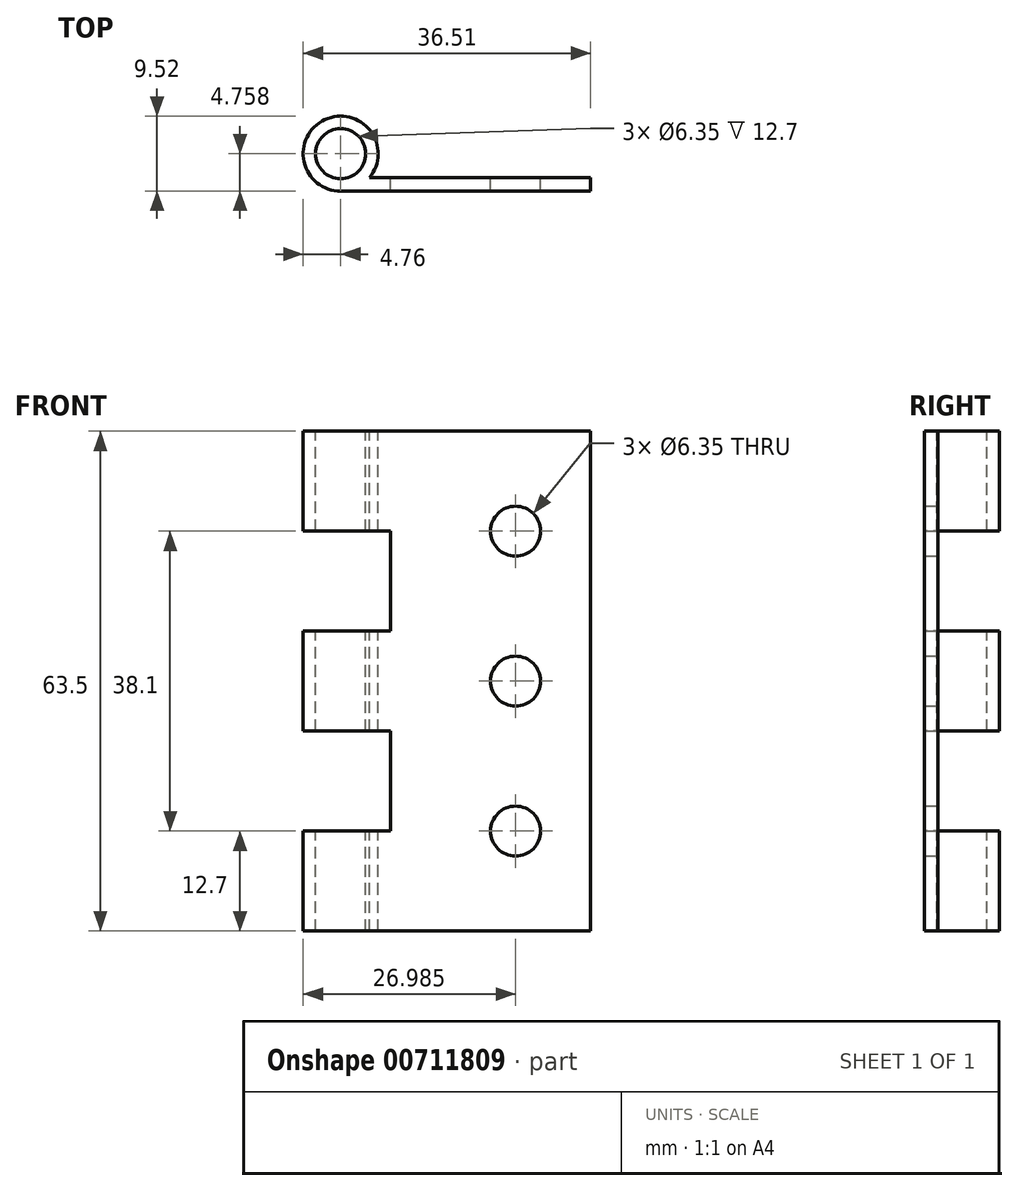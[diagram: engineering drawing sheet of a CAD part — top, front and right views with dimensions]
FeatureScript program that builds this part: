
annotation { "Feature Type Name" : "Feature", "Feature Type Description" : "" }
export const myFeature = defineFeature(function(context is Context, id is Id, definition is map)
    precondition{}
    {
        {
            var Q0;
            Q0=qCreatedBy(makeId("Front.planeOp"),FACE);
            var sketch = newSketch(context, id + "F0", { "sketchPlane" : qUnion([Q0])});
            skLineSegment(sketch, "E0.bottom", {"start": v(0, 0) * mm, "end": v(25.4, 0) * mm});
            skLineSegment(sketch, "E0.top", {"start": v(0, 63.5) * mm, "end": v(25.4, 63.5) * mm});
            skLineSegment(sketch, "E0.left", {"start": v(0, 0) * mm, "end": v(0, 63.5) * mm});
            skLineSegment(sketch, "E0.right", {"start": v(25.4, 0) * mm, "end": v(25.4, 63.5) * mm});
            skLineSegment(sketch, "E1.bottom", {"start": v(0, 63.5) * mm, "end": v(-9.53, 63.5) * mm});
            skLineSegment(sketch, "E1.top", {"start": v(0, 50.8) * mm, "end": v(-9.53, 50.8) * mm});
            skLineSegment(sketch, "E1.left", {"start": v(0, 63.5) * mm, "end": v(0, 50.8) * mm});
            skLineSegment(sketch, "E1.right", {"start": v(-9.53, 63.5) * mm, "end": v(-9.53, 50.8) * mm});
            skLineSegment(sketch, "E2.bottom", {"start": v(0, 0) * mm, "end": v(-9.52, 0) * mm});
            skLineSegment(sketch, "E2.top", {"start": v(0, 12.7) * mm, "end": v(-9.53, 12.7) * mm});
            skLineSegment(sketch, "E2.left", {"start": v(0, 0) * mm, "end": v(0, 12.7) * mm});
            skLineSegment(sketch, "E2.right", {"start": v(-9.52, 0) * mm, "end": v(-9.53, 12.7) * mm});
            skLineSegment(sketch, "E3.bottom", {"start": v(0, 38.1) * mm, "end": v(-9.53, 38.1) * mm});
            skLineSegment(sketch, "E3.top", {"start": v(0, 25.4) * mm, "end": v(-9.53, 25.4) * mm});
            skLineSegment(sketch, "E3.left", {"start": v(0, 38.1) * mm, "end": v(0, 25.4) * mm});
            skLineSegment(sketch, "E3.right", {"start": v(-9.53, 38.1) * mm, "end": v(-9.53, 25.4) * mm});
            skCircle(sketch, "E4", {"center": v(15.87, 50.8) * mm, "radius": 3.18 * mm});
            skCircle(sketch, "E5", {"center": v(15.88, 31.75) * mm, "radius": 3.18 * mm});
            skCircle(sketch, "E6", {"center": v(15.88, 12.7) * mm, "radius": 3.18 * mm});
            skSolve(sketch);
        }
        {
            var Q0;
            Q0 = qSketchRegion(id + "F0", true);
            extrude(context, id + "F1", {"entities" : qUnion([Q0]), "depth" : 1.71 * mm, "offsetDistance" : 25.4 * mm});
        }
        {
            var Q0;
            Q0=makeQuery(id+"F1.opExtrude","SWEPT_FACE",FACE,{"disambiguationData":[OSD([sQuery(id+"F0.wireOp",EDGE,"E0.top"),sQuery(id+"F0.wireOp",EDGE,"E1.bottom")])]});
            var sketch = newSketch(context, id + "F2", { "sketchPlane" : qUnion([Q0])});
            skCircle(sketch, "E7", {"center": v(-6.35, 3.05) * mm, "radius": 4.76 * mm});
            skSolve(sketch);
        }
        {
            var Q0;
            Q0 = qSketchRegion(id + "F2", true);
            extrude(context, id + "F3", {"entities" : qUnion([Q0]), "operationType" : NewBodyOperationType.ADD, "oppositeDirection" : true, "depth" : 63.5 * mm, "offsetDistance" : 25.4 * mm});
        }
        {
            var Q0;
            Q0=makeQuery(id+"F3.boolean.opBoolean","MERGE",FACE,{"derivedFrom":[makeQuery(id+"F1.opExtrude","SWEPT_FACE",FACE,{"disambiguationData":[OSD([sQuery(id+"F0.wireOp",EDGE,"E0.top"),sQuery(id+"F0.wireOp",EDGE,"E1.bottom")])]}),makeQuery(id+"F3.opExtrude","CAP_FACE",FACE,{"disambiguationData":[OSD([sQuery(id+"F2.wireOp",EDGE,"E7")])],"isStart":true})]});
            var sketch = newSketch(context, id + "F4", { "sketchPlane" : qUnion([Q0])});
            skArc(sketch, "E8", {"start": v(-9.53, -0.5) * mm, "mid": v(-8.05, -1.4) * mm, "end": v(-6.35, -1.71) * mm});
            skLineSegment(sketch, "E9", {"start": v(-9.53, -1.71) * mm, "end": v(-9.53, -0.5) * mm});
            skLineSegment(sketch, "E10", {"start": v(-9.53, -1.71) * mm, "end": v(-6.35, -1.71) * mm});
            skCircle(sketch, "E11", {"center": v(-6.35, 3.05) * mm, "radius": 3.18 * mm});
            skSolve(sketch);
        }
        {
            var Q0;
            Q0=makeQuery(id+"F4.imprint","IMPRINT",FACE,{"disambiguationData":[TD([[makeQuery(id+"F4.imprint","IMPRINT",EDGE,{"derivedFrom":sQuery(id+"F4.wireOp",EDGE,"E8")}),-1.0]])]});
            var Q1;
            Q1=makeQuery(id+"F4.imprint","IMPRINT",FACE,{"disambiguationData":[TD([[makeQuery(id+"F4.imprint","IMPRINT",EDGE,{"derivedFrom":sQuery(id+"F4.wireOp",EDGE,"E11")}),1.0]])]});
            extrude(context, id + "F5", {"entities" : qUnion([Q0, Q1]), "operationType" : NewBodyOperationType.REMOVE, "endBound" : BoundingType.THROUGH_ALL, "oppositeDirection" : true, "depth" : 25.4 * mm, "offsetDistance" : 25.4 * mm});
        }
        {
            var Q0;
            Q0=makeQuery(id+"F1.opExtrude","CAP_FACE",FACE,{"disambiguationData":[OSD([sQuery(id+"F0.wireOp",EDGE,"E0.bottom"),sQuery(id+"F0.wireOp",EDGE,"E0.top"),sQuery(id+"F0.wireOp",EDGE,"E0.left"),sQuery(id+"F0.wireOp",EDGE,"E0.right"),sQuery(id+"F0.wireOp",EDGE,"E1.bottom"),sQuery(id+"F0.wireOp",EDGE,"E1.top"),sQuery(id+"F0.wireOp",EDGE,"E1.right"),sQuery(id+"F0.wireOp",EDGE,"E2.bottom"),sQuery(id+"F0.wireOp",EDGE,"E2.top"),sQuery(id+"F0.wireOp",EDGE,"E2.right"),sQuery(id+"F0.wireOp",EDGE,"E3.bottom"),sQuery(id+"F0.wireOp",EDGE,"E3.top"),sQuery(id+"F0.wireOp",EDGE,"E3.right"),sQuery(id+"F0.wireOp",EDGE,"E4"),sQuery(id+"F0.wireOp",EDGE,"E5"),sQuery(id+"F0.wireOp",EDGE,"E6")])],"isStart":false});
            var sketch = newSketch(context, id + "F6", { "sketchPlane" : qUnion([Q0])});
            skLineSegment(sketch, "E12.bottom", {"start": v(0, 50.8) * mm, "end": v(-12.39, 50.8) * mm});
            skLineSegment(sketch, "E12.top", {"start": v(0, 38.1) * mm, "end": v(-12.39, 38.1) * mm});
            skLineSegment(sketch, "E12.left", {"start": v(0, 50.8) * mm, "end": v(0, 38.1) * mm});
            skLineSegment(sketch, "E12.right", {"start": v(-12.39, 50.8) * mm, "end": v(-12.39, 38.1) * mm});
            skLineSegment(sketch, "E13.bottom", {"start": v(0, 25.4) * mm, "end": v(-12.61, 25.4) * mm});
            skLineSegment(sketch, "E13.top", {"start": v(0, 12.7) * mm, "end": v(-12.61, 12.7) * mm});
            skLineSegment(sketch, "E13.left", {"start": v(0, 25.4) * mm, "end": v(0, 12.7) * mm});
            skLineSegment(sketch, "E13.right", {"start": v(-12.61, 25.4) * mm, "end": v(-12.61, 12.7) * mm});
            skSolve(sketch);
        }
        {
            var Q0;
            Q0 = qSketchRegion(id + "F6", true);
            extrude(context, id + "F7", {"entities" : qUnion([Q0]), "operationType" : NewBodyOperationType.REMOVE, "oppositeDirection" : true, "depth" : 25.4 * mm, "offsetDistance" : 25.4 * mm});
        }
    });
